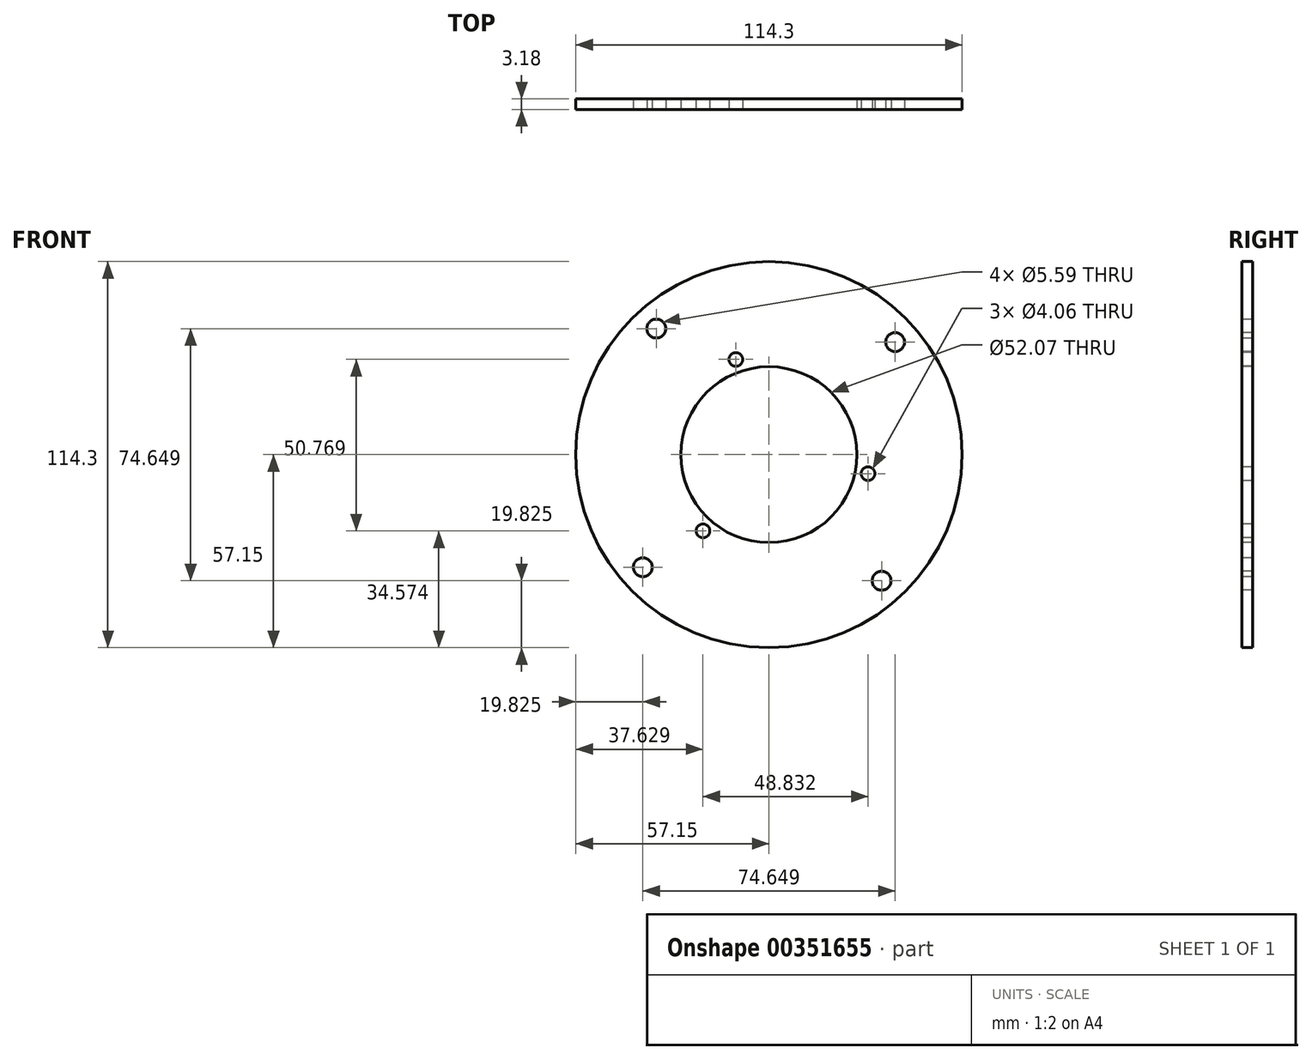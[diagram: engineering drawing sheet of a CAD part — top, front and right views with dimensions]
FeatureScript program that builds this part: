
annotation { "Feature Type Name" : "Feature", "Feature Type Description" : "" }
export const myFeature = defineFeature(function(context is Context, id is Id, definition is map)
    precondition{}
    {
        {
            var Q0;
            Q0=qCreatedBy(makeId("Front.planeOp"),FACE);
            var sketch = newSketch(context, id + "F0", { "sketchPlane" : qUnion([Q0])});
            skCircle(sketch, "E0", {"center": v(0, 0) * mm, "radius": 57.15 * mm});
            skSolve(sketch);
        }
        {
            var Q0;
            Q0=makeQuery(id+"F0.imprint","IMPRINT",FACE,{"disambiguationData":[TD([[makeQuery(id+"F0.imprint","IMPRINT",EDGE,{"derivedFrom":sQuery(id+"F0.wireOp",EDGE,"E0")}),1.0]])]});
            extrude(context, id + "F1", {"entities" : qUnion([Q0]), "depth" : 3.17 * mm});
        }
        {
            var Q0;
            Q0=makeQuery(id+"F1.opExtrude","CAP_FACE",FACE,{"disambiguationData":[OSD([sQuery(id+"F0.wireOp",EDGE,"E0")])],"isStart":false});
            var sketch = newSketch(context, id + "F2", { "sketchPlane" : qUnion([Q0])});
            skCircle(sketch, "E1", {"center": v(0, 0) * mm, "radius": 50.04 * mm, "construction": true});
            skCircle(sketch, "E2", {"center": v(-33.33, 37.32) * mm, "radius": 2.8 * mm});
            skCircle(sketch, "E3.1.0", {"center": v(-37.32, -33.33) * mm, "radius": 2.8 * mm});
            skCircle(sketch, "E3.2.0", {"center": v(33.33, -37.32) * mm, "radius": 2.8 * mm});
            skCircle(sketch, "E3.3.0", {"center": v(37.32, 33.33) * mm, "radius": 2.8 * mm});
            skSolve(sketch);
        }
        {
            var Q0;
            Q0 = qSketchRegion(id + "F2", true);
            extrude(context, id + "F3", {"entities" : qUnion([Q0]), "operationType" : NewBodyOperationType.REMOVE, "oppositeDirection" : true, "depth" : 25.4 * mm});
        }
        {
            var Q0;
            Q0=makeQuery(id+"F2.imprint","IMPRINT",FACE,{"disambiguationData":[TD([[makeQuery(id+"F2.imprint","IMPRINT",EDGE,{"derivedFrom":sQuery(id+"F2.wireOp",EDGE,"E2")}),-1.0]])]});
            var sketch = newSketch(context, id + "F4", { "sketchPlane" : qUnion([Q0])});
            skCircle(sketch, "E4", {"center": v(0, 0) * mm, "radius": 26.04 * mm});
            skCircle(sketch, "E5", {"center": v(0, 0) * mm, "radius": 29.85 * mm, "construction": true});
            skCircle(sketch, "E6", {"center": v(-9.8, 28.2) * mm, "radius": 2.03 * mm});
            skCircle(sketch, "E7.1.0", {"center": v(-19.52, -22.58) * mm, "radius": 2.03 * mm});
            skCircle(sketch, "E7.2.0", {"center": v(29.31, -5.62) * mm, "radius": 2.03 * mm});
            skSolve(sketch);
        }
        {
            var Q0;
            Q0 = qSketchRegion(id + "F4", true);
            extrude(context, id + "F5", {"entities" : qUnion([Q0]), "operationType" : NewBodyOperationType.REMOVE, "oppositeDirection" : true, "depth" : 25.4 * mm});
        }
    });
